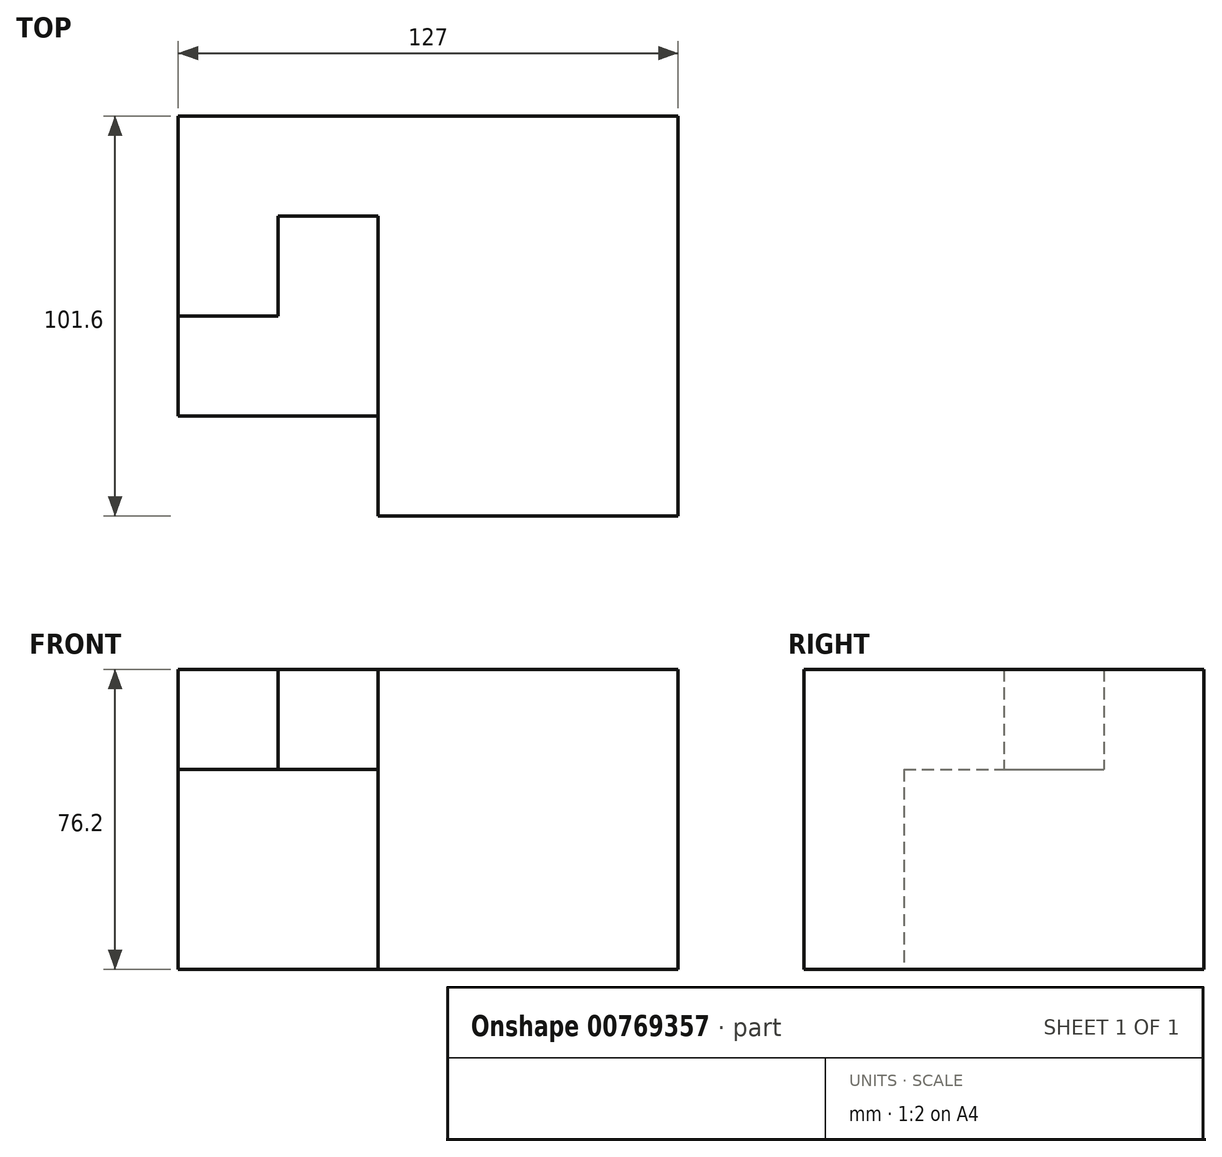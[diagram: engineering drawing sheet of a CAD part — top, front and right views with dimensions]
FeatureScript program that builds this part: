
annotation { "Feature Type Name" : "Feature", "Feature Type Description" : "" }
export const myFeature = defineFeature(function(context is Context, id is Id, definition is map)
    precondition{}
    {
        {
            var Q0;
            Q0=qCreatedBy(makeId("Front.planeOp"),FACE);
            var sketch = newSketch(context, id + "F0", { "sketchPlane" : qUnion([Q0])});
            skLineSegment(sketch, "E0.bottom", {"start": v(-127, 76.2) * mm, "end": v(0, 76.2) * mm});
            skLineSegment(sketch, "E0.top", {"start": v(-127, 0) * mm, "end": v(0, 0) * mm});
            skLineSegment(sketch, "E0.left", {"start": v(-127, 76.2) * mm, "end": v(-127, 0) * mm});
            skLineSegment(sketch, "E0.right", {"start": v(0, 76.2) * mm, "end": v(0, 0) * mm});
            skLineSegment(sketch, "E1", {"start": v(-76.2, 76.2) * mm, "end": v(-76.2, 0) * mm});
            skLineSegment(sketch, "E2", {"start": v(-76.2, 50.8) * mm, "end": v(-127, 50.8) * mm});
            skLineSegment(sketch, "E3", {"start": v(-101.6, 76.2) * mm, "end": v(-101.6, 50.8) * mm});
            skSolve(sketch);
        }
        {
            var Q0;
            {var subQ3=sQuery(id+"F0.wireOp",EDGE,"E3");Q0=makeQuery(id+"F0.imprint","IMPRINT",FACE,{"disambiguationData":[TD([[makeQuery(id+"F0.imprint","IMPRINT",EDGE,{"derivedFrom":subQ3}),1.0]])]});}
            extrude(context, id + "F1", {"entities" : qUnion([Q0]), "depth" : 25.4 * mm, "offsetDistance" : 25.4 * mm});
        }
        {
            var Q0;
            {var subQ3=sQuery(id+"F0.wireOp",EDGE,"E3");Q0=makeQuery(id+"F0.imprint","IMPRINT",FACE,{"disambiguationData":[TD([[makeQuery(id+"F0.imprint","IMPRINT",EDGE,{"derivedFrom":subQ3}),-1.0]])]});}
            extrude(context, id + "F2", {"entities" : qUnion([Q0]), "operationType" : NewBodyOperationType.ADD, "depth" : 50.8 * mm, "offsetDistance" : 25.4 * mm});
        }
        {
            var Q0;
            {var subQ4=sQuery(id+"F0.wireOp",EDGE,"E0.top");var subQ6=sQuery(id+"F0.wireOp",EDGE,"E0.left");var subQ7=makeQuery(id+"F0.imprint","INTERSECT",VERTEX,{"derivedFrom":[subQ4,subQ6]});Q0=makeQuery(id+"F0.imprint","IMPRINT",FACE,{"disambiguationData":[TD([[makeQuery(id+"F0.imprint","IMPRINT",EDGE,{"disambiguationData":[TD([[subQ7,-1.0]])],"derivedFrom":subQ4}),1.0]])]});}
            extrude(context, id + "F3", {"entities" : qUnion([Q0]), "operationType" : NewBodyOperationType.ADD, "depth" : 76.2 * mm, "offsetDistance" : 25.4 * mm});
        }
        {
            var Q0;
            {var subQ4=sQuery(id+"F0.wireOp",EDGE,"E0.right");Q0=makeQuery(id+"F0.imprint","IMPRINT",FACE,{"disambiguationData":[TD([[makeQuery(id+"F0.imprint","IMPRINT",EDGE,{"derivedFrom":subQ4}),-1.0]])]});}
            extrude(context, id + "F4", {"entities" : qUnion([Q0]), "operationType" : NewBodyOperationType.ADD, "depth" : 101.6 * mm, "offsetDistance" : 25.4 * mm});
        }
    });
